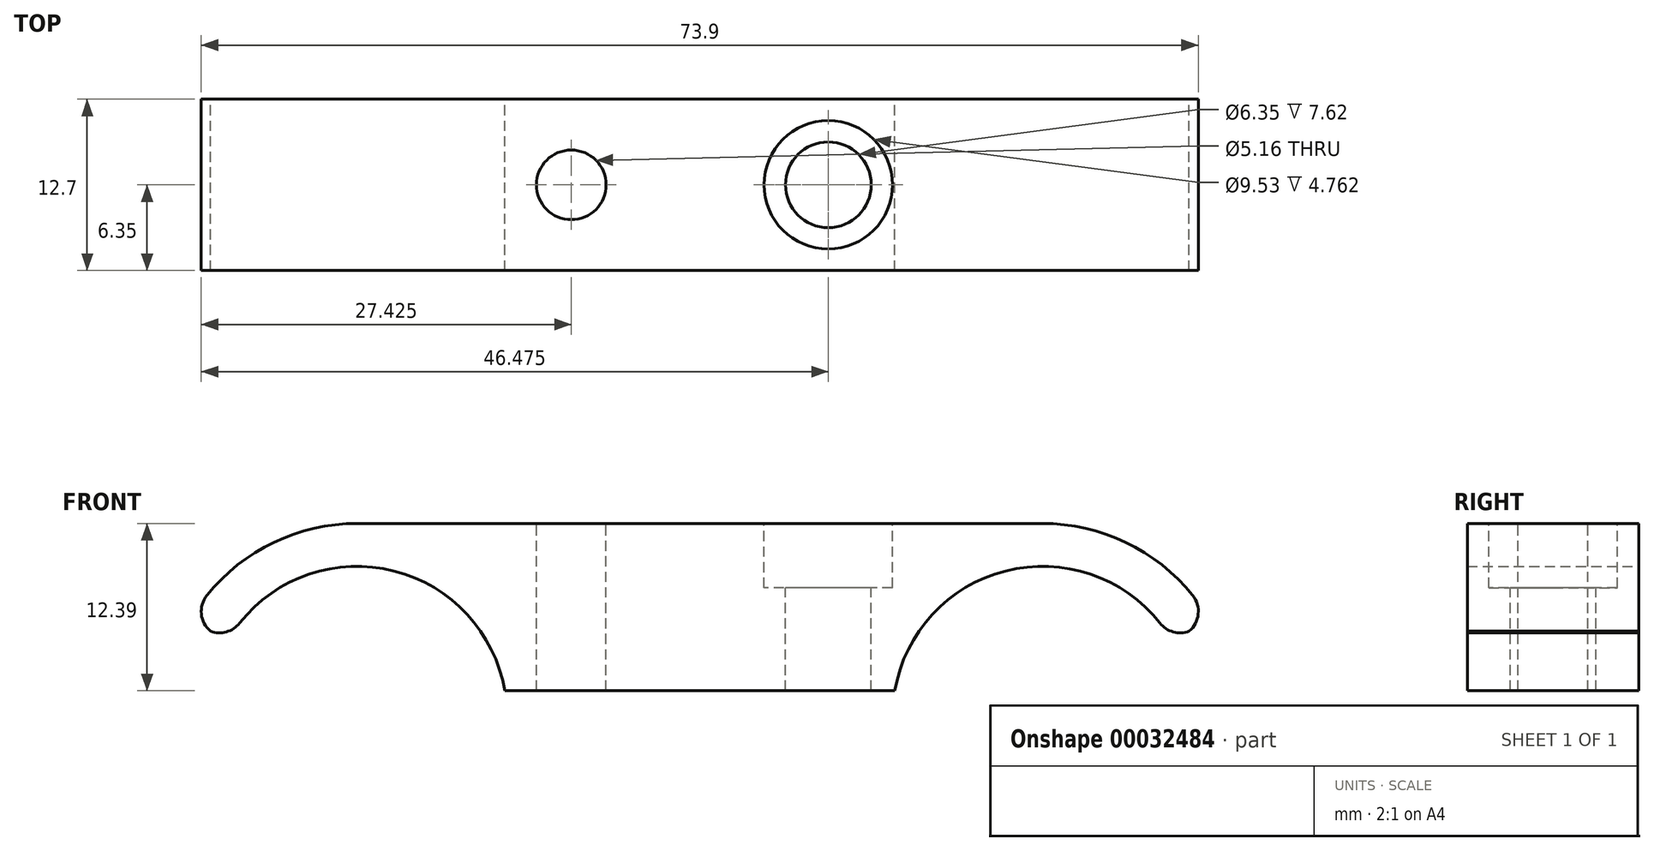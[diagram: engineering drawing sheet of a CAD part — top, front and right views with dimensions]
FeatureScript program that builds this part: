
annotation { "Feature Type Name" : "Feature", "Feature Type Description" : "" }
export const myFeature = defineFeature(function(context is Context, id is Id, definition is map)
    precondition{}
    {
        {
            var Q0;
            Q0=qCreatedBy(makeId("Front.planeOp"),FACE);
            var sketch = newSketch(context, id + "F0", { "sketchPlane" : qUnion([Q0])});
            skArc(sketch, "E0", {"start": v(-14.29, 0) * mm, "mid": v(-22.52, 10.73) * mm, "end": v(-35.02, 5.56) * mm});
            skArc(sketch, "E1.0", {"start": v(-25.4, 14.29) * mm, "mid": v(-32.54, 12.37) * mm, "end": v(-37.77, 7.14) * mm});
            skLineSegment(sketch, "E2", {"start": v(-25.4, 14.29) * mm, "end": v(0, 14.29) * mm});
            skLineSegment(sketch, "E3", {"start": v(-14.29, 0) * mm, "end": v(0, 0) * mm, "construction": true});
            skLineSegment(sketch, "E4", {"start": v(-14.29, 0) * mm, "end": v(0, 0) * mm});
            skLineSegment(sketch, "E5", {"start": v(-35.02, 5.56) * mm, "end": v(-37.77, 7.14) * mm});
            skLineSegment(sketch, "E6", {"start": v(0, 19.2) * mm, "end": v(0, 0) * mm, "construction": true});
            skPoint(sketch, "E7.center.orphan", {"position": v(25.4, 0) * mm});
            skLineSegment(sketch, "E8.MirrorCS", {"start": v(25.4, 14.29) * mm, "end": v(0, 14.29) * mm});
            skArc(sketch, "E9.MirrorCS", {"start": v(25.4, 14.29) * mm, "mid": v(32.54, 12.37) * mm, "end": v(37.77, 7.14) * mm});
            skLineSegment(sketch, "E10.MirrorCS", {"start": v(35.02, 5.56) * mm, "end": v(37.77, 7.14) * mm});
            skArc(sketch, "E11.MirrorCS", {"start": v(14.29, 0) * mm, "mid": v(22.52, 10.73) * mm, "end": v(35.02, 5.56) * mm});
            skLineSegment(sketch, "E12.MirrorCS", {"start": v(14.29, 0) * mm, "end": v(0, 0) * mm});
            skSolve(sketch);
        }
        {
            var Q0;
            Q0 = qSketchRegion(id + "F0", true);
            extrude(context, id + "F1", {"entities" : qUnion([Q0]), "depth" : 12.7 * mm});
        }
        {
            var Q0;
            Q0=makeQuery(id+"F1.opExtrude","SWEPT_FACE",FACE,{"disambiguationData":[OSD([sQuery(id+"F0.wireOp",EDGE,"E2"),sQuery(id+"F0.wireOp",EDGE,"E8.MirrorCS")])]});
            var sketch = newSketch(context, id + "F2", { "sketchPlane" : qUnion([Q0])});
            skCircle(sketch, "E13", {"center": v(9.53, -6.35) * mm, "radius": 3.18 * mm});
            skCircle(sketch, "E14", {"center": v(-9.52, -6.35) * mm, "radius": 2.58 * mm});
            skLineSegment(sketch, "E15", {"start": v(0, 2.13) * mm, "end": v(0, -12.45) * mm, "construction": true});
            skPoint(sketch, "E15.endSnap0", {"position": v(0, -12.7) * mm});
            skCircle(sketch, "E16", {"center": v(9.53, -6.35) * mm, "radius": 4.76 * mm});
            skLineSegment(sketch, "E17.right", {"start": v(0, 0) * mm, "end": v(0, -12.7) * mm});
            skSolve(sketch);
        }
        {
            var Q0;
            Q0=makeQuery(id+"F2.imprint","IMPRINT",FACE,{"disambiguationData":[TD([[makeQuery(id+"F2.imprint","IMPRINT",EDGE,{"derivedFrom":sQuery(id+"F2.wireOp",EDGE,"E13")}),1.0]])]});
            var Q1;
            Q1=makeQuery(id+"F2.imprint","IMPRINT",FACE,{"disambiguationData":[TD([[makeQuery(id+"F2.imprint","IMPRINT",EDGE,{"derivedFrom":sQuery(id+"F2.wireOp",EDGE,"E14")}),1.0]])]});
            extrude(context, id + "F3", {"entities" : qUnion([Q0, Q1]), "operationType" : NewBodyOperationType.REMOVE, "endBound" : BoundingType.THROUGH_ALL, "oppositeDirection" : true, "depth" : 25.4 * mm});
        }
        {
            var Q0;
            Q0=makeQuery(id+"F2.imprint","IMPRINT",FACE,{"disambiguationData":[TD([[makeQuery(id+"F2.imprint","IMPRINT",EDGE,{"derivedFrom":sQuery(id+"F2.wireOp",EDGE,"E13")}),-1.0]])]});
            extrude(context, id + "F4", {"entities" : qUnion([Q0]), "operationType" : NewBodyOperationType.REMOVE, "oppositeDirection" : true, "depth" : 4.76 * mm});
        }
        {
            var Q0;
            Q0=makeQuery(id+"F1.opExtrude","CAP_FACE",FACE,{"disambiguationData":[OSD([sQuery(id+"F0.wireOp",EDGE,"E0"),sQuery(id+"F0.wireOp",EDGE,"E1.0"),sQuery(id+"F0.wireOp",EDGE,"E2"),sQuery(id+"F0.wireOp",EDGE,"E4"),sQuery(id+"F0.wireOp",EDGE,"E5"),sQuery(id+"F0.wireOp",EDGE,"E8.MirrorCS"),sQuery(id+"F0.wireOp",EDGE,"E9.MirrorCS"),sQuery(id+"F0.wireOp",EDGE,"E10.MirrorCS"),sQuery(id+"F0.wireOp",EDGE,"E11.MirrorCS"),sQuery(id+"F0.wireOp",EDGE,"E12.MirrorCS")])],"isStart":false});
            var sketch = newSketch(context, id + "F5", { "sketchPlane" : qUnion([Q0])});
            skLineSegment(sketch, "E18", {"start": v(-24.32, 14.29) * mm, "end": v(-14.35, 9.48) * mm});
            skSolve(sketch);
        }
        {
            var Q0;
            Q0=sQuery(id+"F5.wireOp",EDGE,"E18");
            cPlane(context, id + "F6", {"entities" : qUnion([Q0]), "cplaneType" : CPlaneType.LINE_ANGLE, "offset" : 152.4 * mm, "angle" : 90 * degree, "width" : 152.4 * mm, "height" : 152.4 * mm});
        }
        {
            var Q0;
            Q0=makeQuery(id+"F1.opExtrude","SWEPT_EDGE",EDGE,{"disambiguationData":[OSD([sQuery(id+"F0.wireOp",EDGE,"E1.0"),sQuery(id+"F0.wireOp",EDGE,"E5")])]});
            var Q1;
            Q1=makeQuery(id+"F1.opExtrude","SWEPT_EDGE",EDGE,{"disambiguationData":[OSD([sQuery(id+"F0.wireOp",EDGE,"E0"),sQuery(id+"F0.wireOp",EDGE,"E5")])]});
            var Q2;
            Q2=makeQuery(id+"F1.opExtrude","SWEPT_EDGE",EDGE,{"disambiguationData":[OSD([sQuery(id+"F0.wireOp",EDGE,"E9.MirrorCS"),sQuery(id+"F0.wireOp",EDGE,"E10.MirrorCS")])]});
            var Q3;
            Q3=makeQuery(id+"F1.opExtrude","SWEPT_EDGE",EDGE,{"disambiguationData":[OSD([sQuery(id+"F0.wireOp",EDGE,"E10.MirrorCS"),sQuery(id+"F0.wireOp",EDGE,"E11.MirrorCS")])]});
            fillet(context, id + "F7", {"entities" : qUnion([Q0, Q1, Q2, Q3]), "radius" : 1.9 * mm, "allowEdgeOverflow" : false});
        }
        {
            var Q0;
            Q0=makeQuery(id+"F1.opExtrude","SWEPT_FACE",FACE,{"disambiguationData":[OSD([sQuery(id+"F0.wireOp",EDGE,"E4"),sQuery(id+"F0.wireOp",EDGE,"E12.MirrorCS")])]});
            var sketch = newSketch(context, id + "F8", { "sketchPlane" : qUnion([Q0])});
            skLineSegment(sketch, "E19.rect.bottom", {"start": v(16.14, -1.93) * mm, "end": v(-16.14, -1.93) * mm});
            skLineSegment(sketch, "E19.rect.top", {"start": v(16.14, 14.05) * mm, "end": v(-16.14, 14.05) * mm});
            skLineSegment(sketch, "E19.rect.left", {"start": v(16.14, -1.93) * mm, "end": v(16.14, 14.05) * mm});
            skLineSegment(sketch, "E19.rect.right", {"start": v(-16.14, -1.93) * mm, "end": v(-16.14, 14.05) * mm});
            skPoint(sketch, "E19.rect.middle", {"position": v(0, 6.06) * mm});
            skSolve(sketch);
        }
        {
            var Q0;
            Q0 = qSketchRegion(id + "F8", true);
            extrude(context, id + "F9", {"entities" : qUnion([Q0]), "operationType" : NewBodyOperationType.REMOVE, "oppositeDirection" : true, "depth" : 1.9 * mm});
        }
    });
